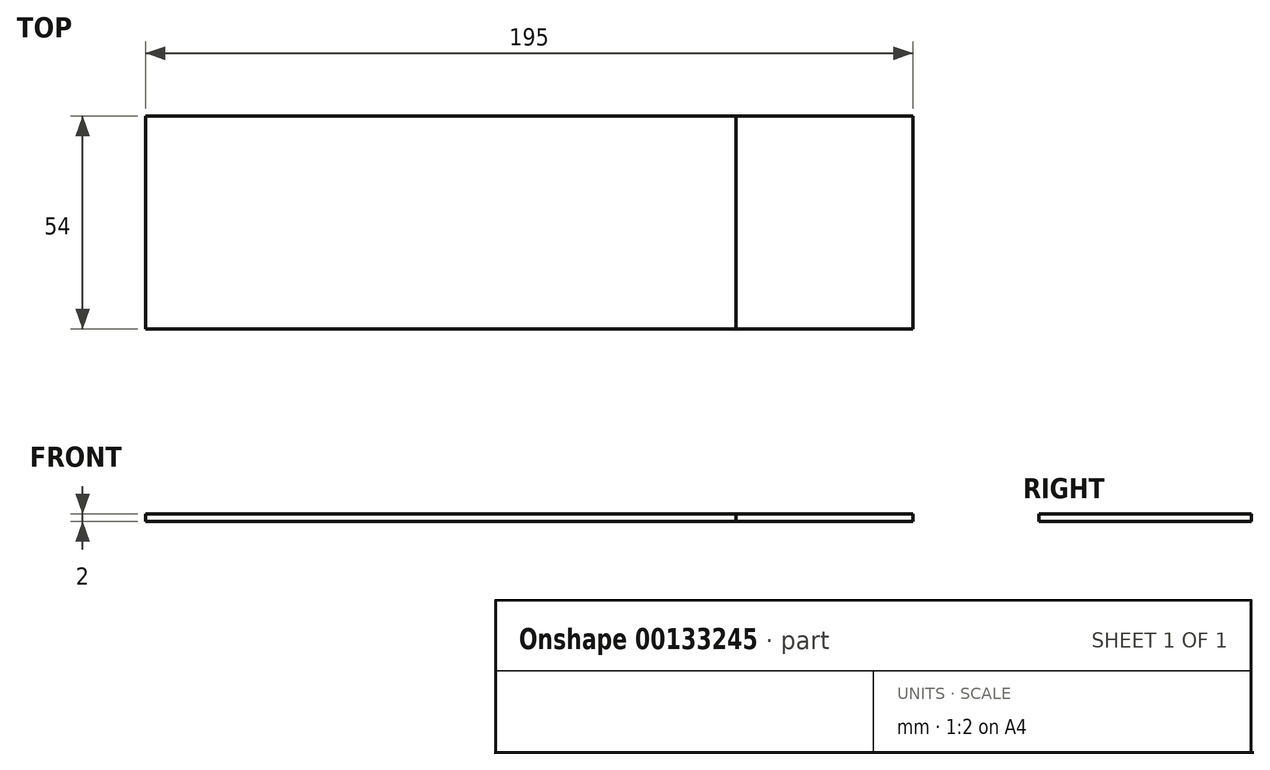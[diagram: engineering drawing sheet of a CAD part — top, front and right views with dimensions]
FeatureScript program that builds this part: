
annotation { "Feature Type Name" : "Feature", "Feature Type Description" : "" }
export const myFeature = defineFeature(function(context is Context, id is Id, definition is map)
    precondition{}
    {
        {
            var Q0;
            Q0=qCreatedBy(makeId("Top.planeOp"),FACE);
            var sketch = newSketch(context, id + "F0", { "sketchPlane" : qUnion([Q0])});
            skLineSegment(sketch, "E0.bottom", {"start": v(-97.5, 54) * mm, "end": v(97.5, 54) * mm});
            skLineSegment(sketch, "E0.top", {"start": v(-97.5, 0) * mm, "end": v(97.5, 0) * mm});
            skLineSegment(sketch, "E0.left", {"start": v(-97.5, 54) * mm, "end": v(-97.5, 0) * mm});
            skLineSegment(sketch, "E0.right", {"start": v(97.5, 54) * mm, "end": v(97.5, 0) * mm});
            skPoint(sketch, "E1", {"position": v(0, 0) * mm});
            skSolve(sketch);
        }
        {
            var Q0;
            Q0=makeQuery(id+"F0.imprint","IMPRINT",FACE,{"disambiguationData":[TD([[makeQuery(id+"F0.imprint","IMPRINT",EDGE,{"derivedFrom":sQuery(id+"F0.wireOp",EDGE,"E0.bottom")}),-1.0]])]});
            extrude(context, id + "F1", {"entities" : qUnion([Q0]), "depth" : 2 * mm});
        }
        {
            var Q0;
            Q0=makeQuery(id+"F1.opExtrude","SWEPT_FACE",FACE,{"disambiguationData":[OSD([sQuery(id+"F0.wireOp",EDGE,"E0.left")])]});
            extrude(context, id + "F2", {"entities" : qUnion([Q0]), "oppositeDirection" : true, "depth" : 150 * mm});
        }
        {
            var Q0;
            Q0=makeQuery(id+"F1.opExtrude","SWEPT_FACE",FACE,{"disambiguationData":[OSD([sQuery(id+"F0.wireOp",EDGE,"E0.right")])]});
            var Q1;
            Q1=makeQuery(id+"F2.opExtrude","CAP_FACE",FACE,{"disambiguationData":[OSD([sQuery(id+"F0.wireOp",EDGE,"E0.left")])],"isStart":false});
            extrude(context, id + "F3", {"entities" : qUnion([Q0]), "endBound" : BoundingType.UP_TO_SURFACE, "oppositeDirection" : true, "endBoundEntityFace" : qUnion([Q1]), "depth" : 25 * mm});
        }
    });
